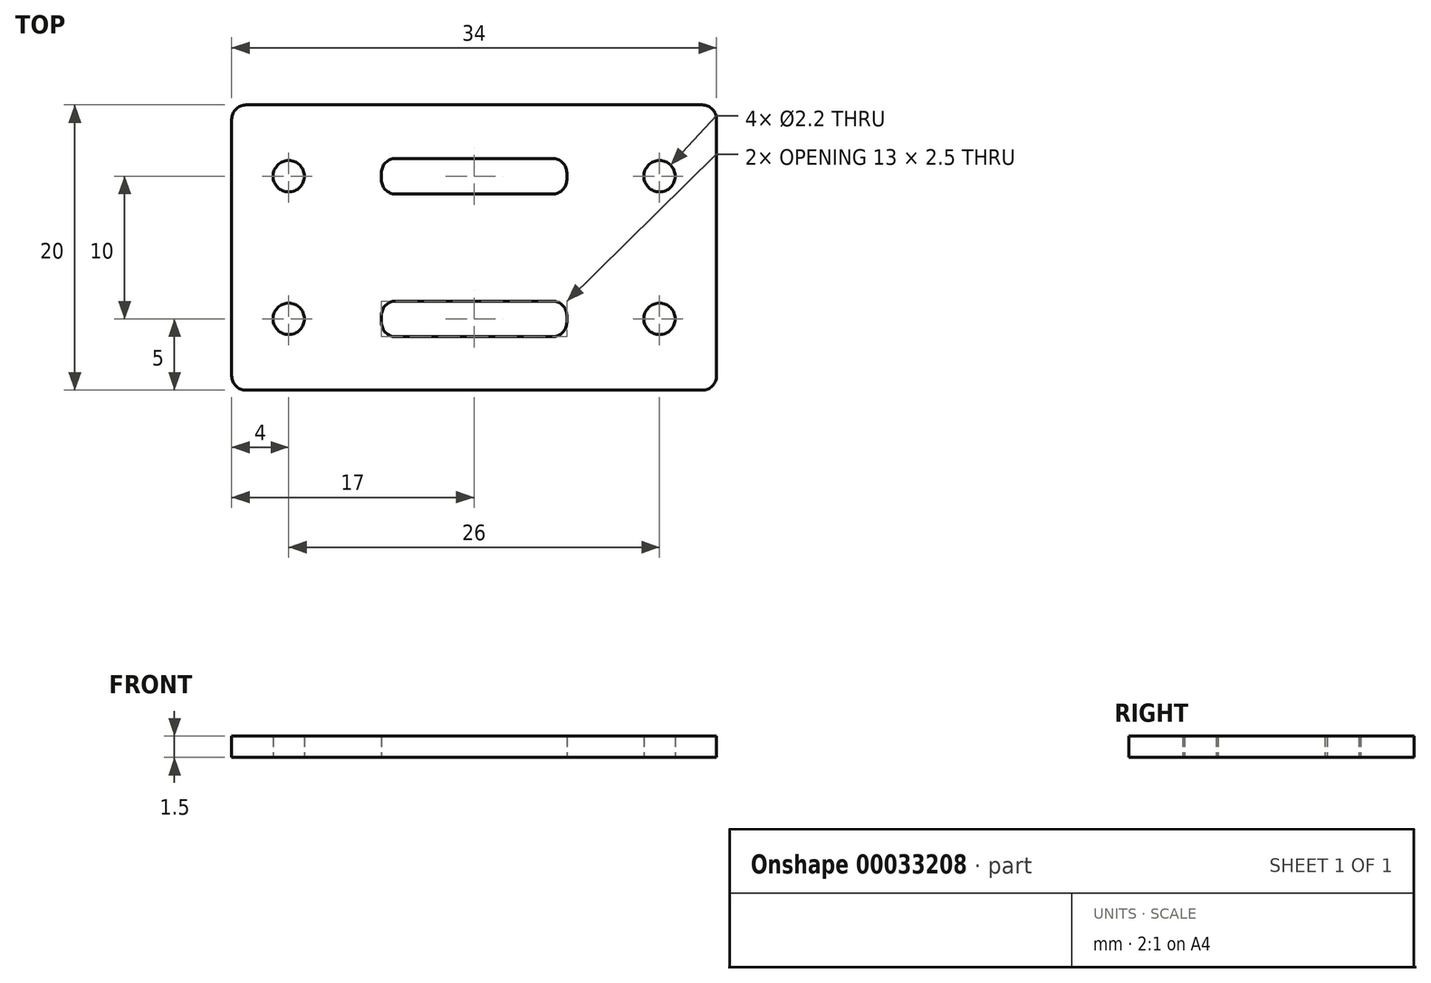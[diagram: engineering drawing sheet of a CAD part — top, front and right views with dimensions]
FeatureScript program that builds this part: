
annotation { "Feature Type Name" : "Feature", "Feature Type Description" : "" }
export const myFeature = defineFeature(function(context is Context, id is Id, definition is map)
    precondition{}
    {
        {
            var Q0;
            Q0=qCreatedBy(makeId("Top.planeOp"),FACE);
            var sketch = newSketch(context, id + "F0", { "sketchPlane" : qUnion([Q0])});
            skLineSegment(sketch, "E0.bottom", {"start": v(16, 10) * mm, "end": v(-16, 10) * mm});
            skLineSegment(sketch, "E0.top", {"start": v(16, -10) * mm, "end": v(-16, -10) * mm});
            skLineSegment(sketch, "E0.left", {"start": v(17, 9) * mm, "end": v(17, -9) * mm});
            skLineSegment(sketch, "E0.right", {"start": v(-17, 9) * mm, "end": v(-17, -9) * mm});
            skPoint(sketch, "E0.middle", {"position": v(0, 0) * mm});
            skCircle(sketch, "E1", {"center": v(13, 5) * mm, "radius": 1.1 * mm});
            skCircle(sketch, "E2.MirrorC", {"center": v(13, -5) * mm, "radius": 1.1 * mm});
            skCircle(sketch, "E3.MirrorC", {"center": v(-13, 5) * mm, "radius": 1.1 * mm});
            skLineSegment(sketch, "E4.bottom", {"start": v(-5.5, 6.25) * mm, "end": v(5.5, 6.25) * mm});
            skLineSegment(sketch, "E4.top", {"start": v(-5.5, 3.75) * mm, "end": v(5.5, 3.75) * mm});
            skLineSegment(sketch, "E4.left", {"start": v(-6.5, 5.25) * mm, "end": v(-6.5, 4.75) * mm});
            skLineSegment(sketch, "E4.right", {"start": v(6.5, 5.25) * mm, "end": v(6.5, 4.75) * mm});
            skPoint(sketch, "E4.middle", {"position": v(0, 5) * mm});
            skPoint(sketch, "E5.visualSharp", {"position": v(-6.5, 6.25) * mm});
            skArc(sketch, "E5.filletArc", {"start": v(-5.5, 6.25) * mm, "mid": v(-6.2, 5.96) * mm, "end": v(-6.5, 5.25) * mm});
            skPoint(sketch, "E6.visualSharp", {"position": v(-6.5, 3.75) * mm});
            skArc(sketch, "E6.filletArc", {"start": v(-6.5, 4.75) * mm, "mid": v(-6.2, 4.04) * mm, "end": v(-5.5, 3.75) * mm});
            skPoint(sketch, "E7.visualSharp", {"position": v(6.5, 6.25) * mm});
            skArc(sketch, "E7.filletArc", {"start": v(6.5, 5.25) * mm, "mid": v(6.2, 5.96) * mm, "end": v(5.5, 6.25) * mm});
            skPoint(sketch, "E8.visualSharp", {"position": v(6.5, 3.75) * mm});
            skArc(sketch, "E8.filletArc", {"start": v(5.5, 3.75) * mm, "mid": v(6.2, 4.04) * mm, "end": v(6.5, 4.75) * mm});
            skLineSegment(sketch, "E9.MirrorCS", {"start": v(-6.5, -5.25) * mm, "end": v(-6.5, -4.75) * mm});
            skLineSegment(sketch, "E10.MirrorCS", {"start": v(6.5, -5.25) * mm, "end": v(6.5, -4.75) * mm});
            skArc(sketch, "E11.MirrorCS", {"start": v(6.5, -5.25) * mm, "mid": v(6.2, -5.96) * mm, "end": v(5.5, -6.25) * mm});
            skArc(sketch, "E12.MirrorCS", {"start": v(-6.5, -4.75) * mm, "mid": v(-6.2, -4.04) * mm, "end": v(-5.5, -3.75) * mm});
            skPoint(sketch, "E13.MirrorP", {"position": v(6.5, -3.75) * mm});
            skPoint(sketch, "E14.MirrorP", {"position": v(6.5, -6.25) * mm});
            skArc(sketch, "E15.MirrorCS", {"start": v(-5.5, -6.25) * mm, "mid": v(-6.2, -5.96) * mm, "end": v(-6.5, -5.25) * mm});
            skArc(sketch, "E16.MirrorCS", {"start": v(5.5, -3.75) * mm, "mid": v(6.2, -4.04) * mm, "end": v(6.5, -4.75) * mm});
            skPoint(sketch, "E17.MirrorP", {"position": v(-6.5, -3.75) * mm});
            skLineSegment(sketch, "E18.MirrorCS", {"start": v(-5.5, -6.25) * mm, "end": v(5.5, -6.25) * mm});
            skPoint(sketch, "E19.MirrorP", {"position": v(0, -5) * mm});
            skLineSegment(sketch, "E20.MirrorCS", {"start": v(-5.5, -3.75) * mm, "end": v(5.5, -3.75) * mm});
            skPoint(sketch, "E21.MirrorP", {"position": v(-6.5, -6.25) * mm});
            skCircle(sketch, "E22.MirrorC", {"center": v(-13, -5) * mm, "radius": 1.1 * mm});
            skPoint(sketch, "E23.visualSharp", {"position": v(-17, 10) * mm});
            skArc(sketch, "E23.filletArc", {"start": v(-16, 10) * mm, "mid": v(-16.7, 9.7) * mm, "end": v(-17, 9) * mm});
            skPoint(sketch, "E24.visualSharp", {"position": v(-17, -10) * mm});
            skArc(sketch, "E24.filletArc", {"start": v(-17, -9) * mm, "mid": v(-16.7, -9.7) * mm, "end": v(-16, -10) * mm});
            skPoint(sketch, "E25.visualSharp", {"position": v(17, -10) * mm});
            skArc(sketch, "E25.filletArc", {"start": v(16, -10) * mm, "mid": v(16.7, -9.7) * mm, "end": v(17, -9) * mm});
            skPoint(sketch, "E26.visualSharp", {"position": v(17, 10) * mm});
            skArc(sketch, "E26.filletArc", {"start": v(17, 9) * mm, "mid": v(16.7, 9.7) * mm, "end": v(16, 10) * mm});
            skSolve(sketch);
        }
        {
            var Q0;
            Q0 = qSketchRegion(id + "F0", true);
            extrude(context, id + "F1", {"entities" : qUnion([Q0]), "depth" : 1.5 * mm});
        }
    });
